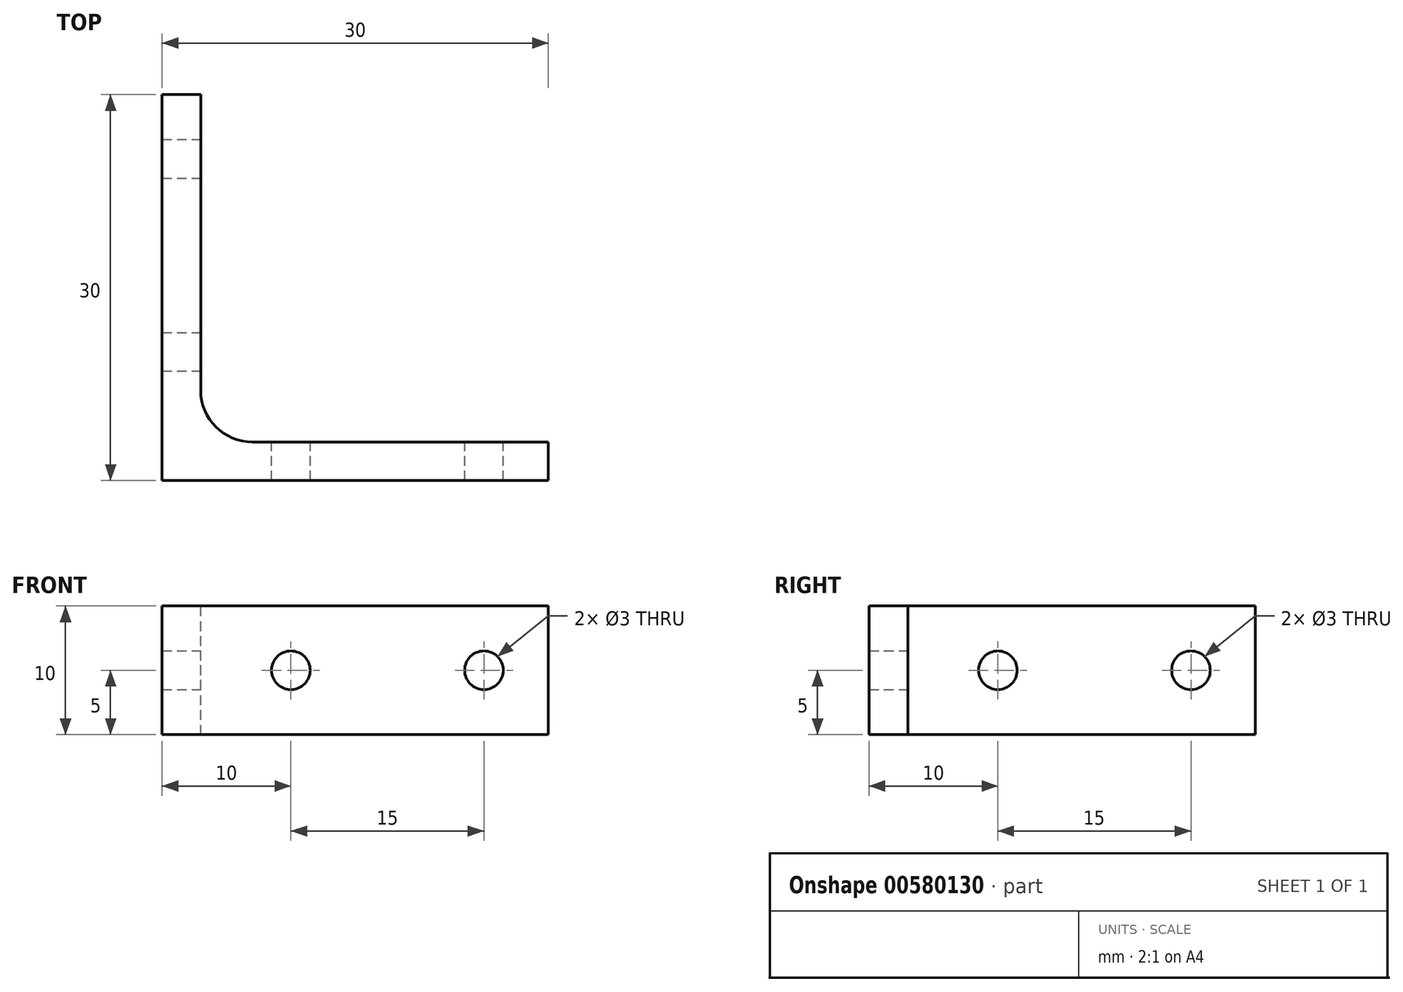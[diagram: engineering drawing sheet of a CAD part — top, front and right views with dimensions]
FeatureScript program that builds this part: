
annotation { "Feature Type Name" : "Feature", "Feature Type Description" : "" }
export const myFeature = defineFeature(function(context is Context, id is Id, definition is map)
    precondition{}
    {
        {
            var Q0;
            Q0=qCreatedBy(makeId("Right.planeOp"),FACE);
            var sketch = newSketch(context, id + "F0", { "sketchPlane" : qUnion([Q0])});
            skLineSegment(sketch, "E0.bottom", {"start": v(0, 30) * mm, "end": v(3, 30) * mm});
            skLineSegment(sketch, "E0.left", {"start": v(0, 30) * mm, "end": v(0, 0) * mm});
            skLineSegment(sketch, "E0.right", {"start": v(3, 30) * mm, "end": v(3, 7) * mm});
            skLineSegment(sketch, "E1.bottom", {"start": v(7, 3) * mm, "end": v(30, 3) * mm});
            skLineSegment(sketch, "E1.right", {"start": v(30, 3) * mm, "end": v(30, 0) * mm});
            skArc(sketch, "E2.filletArc", {"start": v(3, 7) * mm, "mid": v(4.17, 4.17) * mm, "end": v(7, 3) * mm});
            skLineSegment(sketch, "E3", {"start": v(0, 0) * mm, "end": v(30, 0) * mm});
            skSolve(sketch);
        }
        {
            var Q0;
            Q0 = qSketchRegion(id + "F0", true);
            extrude(context, id + "F1", {"entities" : qUnion([Q0]), "endBound" : BoundingType.SYMMETRIC, "depth" : 10 * mm, "offsetDistance" : 25 * mm});
        }
        {
            var Q0;
            Q0=makeQuery(id+"F1.opExtrude","SWEPT_FACE",FACE,{"disambiguationData":[OSD([sQuery(id+"F0.wireOp",EDGE,"E1.bottom")])]});
            var sketch = newSketch(context, id + "F2", { "sketchPlane" : qUnion([Q0])});
            skPoint(sketch, "E4", {"position": v(0, 25) * mm});
            skPoint(sketch, "E5", {"position": v(0, 10) * mm});
            skSolve(sketch);
        }
        {
            var Q0;
            Q0=makeQuery(id+"F1.opExtrude","SWEPT_FACE",FACE,{"disambiguationData":[OSD([sQuery(id+"F0.wireOp",EDGE,"E0.right")])]});
            var sketch = newSketch(context, id + "F3", { "sketchPlane" : qUnion([Q0])});
            skPoint(sketch, "E6", {"position": v(0, 25) * mm});
            skPoint(sketch, "E7", {"position": v(0, 10) * mm});
            skSolve(sketch);
        }
        {
            var Q0;
            Q0=sQuery(id+"F2.wireOp",VERTEX,"E4");
            var Q1;
            Q1=sQuery(id+"F2.wireOp",VERTEX,"E5");
            var Q2;
            Q2=sQuery(id+"F3.wireOp",VERTEX,"E6");
            var Q3;
            Q3=sQuery(id+"F3.wireOp",VERTEX,"E7");
            var Q4;
            Q4=makeQuery(id+"F1.opExtrude","SWEPT_BODY",BODY,{"disambiguationData":[OSD([sQuery(id+"F0.wireOp",EDGE,"E0.bottom"),sQuery(id+"F0.wireOp",EDGE,"E0.left"),sQuery(id+"F0.wireOp",EDGE,"E0.right"),sQuery(id+"F0.wireOp",EDGE,"E1.bottom"),sQuery(id+"F0.wireOp",EDGE,"E1.right"),sQuery(id+"F0.wireOp",EDGE,"E2.filletArc"),sQuery(id+"F0.wireOp",EDGE,"E3")])]});
            hole(context, id + "F4", {"style" : HoleStyle.SIMPLE, "endStyle" : HoleEndStyle.THROUGH, "holeDiameter" : 3 * mm, "majorDiameter" : 5 * mm, "isTappedThrough" : true, "tappedDepth" : 12 * mm, "tapClearance" : 3, "locations" : qUnion([Q0, Q1, Q2, Q3]), "scope" : qUnion([Q4])});
        }
        {
            var Q0;
            Q0=makeQuery(id+"F1.opExtrude","SWEPT_BODY",BODY,{"disambiguationData":[OSD([sQuery(id+"F0.wireOp",EDGE,"E0.bottom"),sQuery(id+"F0.wireOp",EDGE,"E0.left"),sQuery(id+"F0.wireOp",EDGE,"E0.right"),sQuery(id+"F0.wireOp",EDGE,"E1.bottom"),sQuery(id+"F0.wireOp",EDGE,"E1.right"),sQuery(id+"F0.wireOp",EDGE,"E2.filletArc"),sQuery(id+"F0.wireOp",EDGE,"E3")])]});
            var Q1;
            Q1=makeQuery(id+"F1.opExtrude","CAP_EDGE",EDGE,{"disambiguationData":[OSD([sQuery(id+"F0.wireOp",EDGE,"E3")])],"isStart":false});
            var Q2;
            Q2=makeQuery(id+"F1.opExtrude","CAP_EDGE",EDGE,{"disambiguationData":[OSD([sQuery(id+"F0.wireOp",EDGE,"E3")])],"isStart":false});
            transform(context, id + "F5", {"entities" : qUnion([Q0]), "transformType" : TransformType.ROTATION, "transformAxis" : qUnion([Q2]), "angle" : 90 * degree, "makeCopy" : false});
        }
    });
